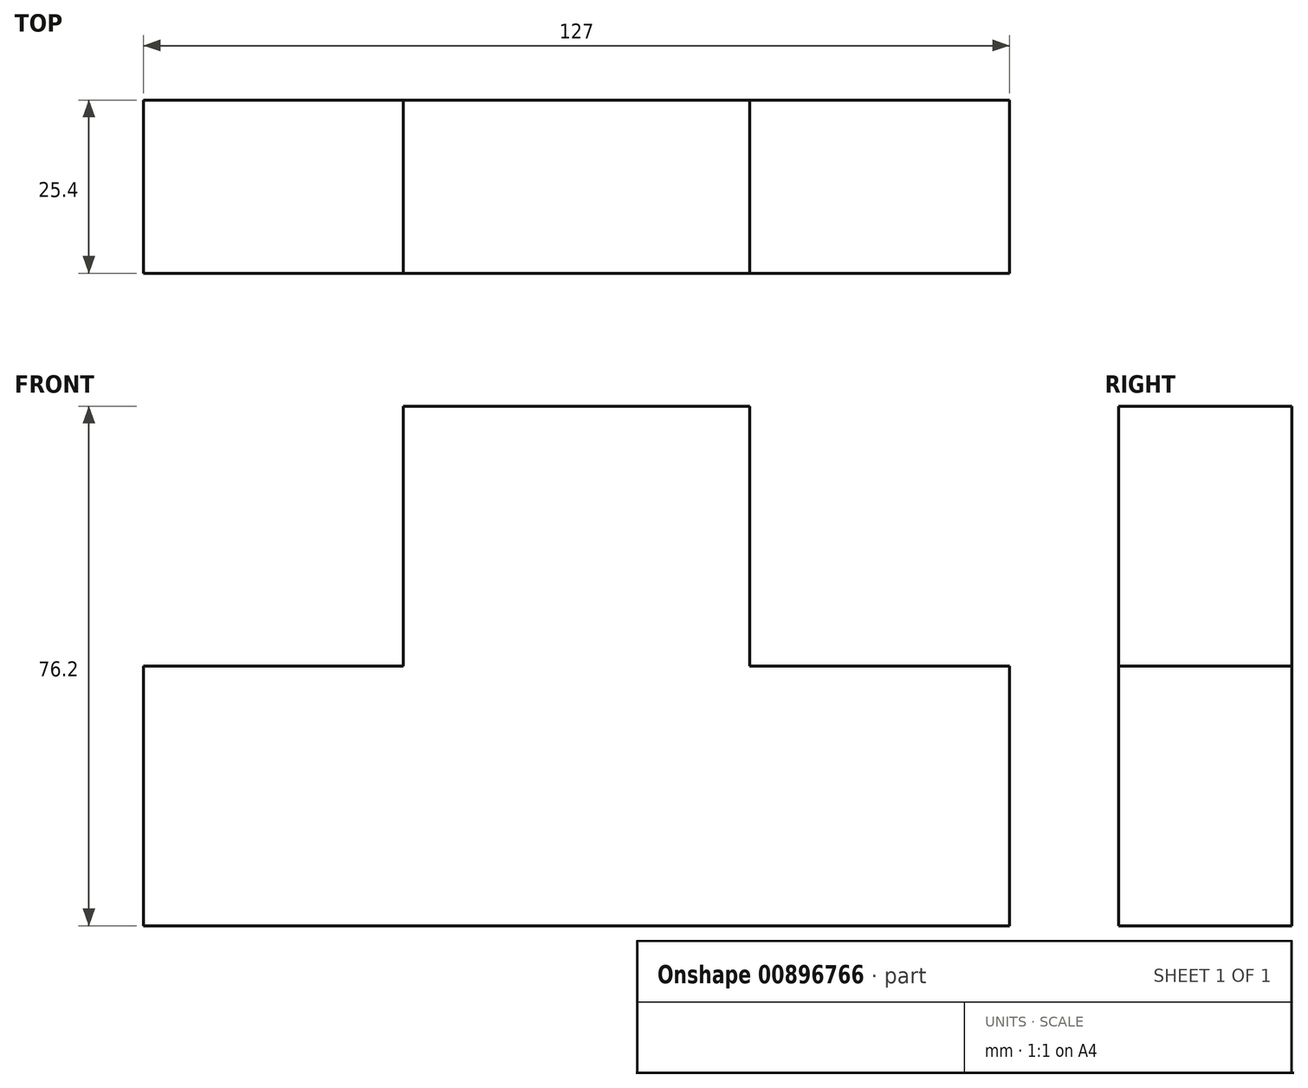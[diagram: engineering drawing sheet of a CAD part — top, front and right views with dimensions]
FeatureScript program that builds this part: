
annotation { "Feature Type Name" : "Feature", "Feature Type Description" : "" }
export const myFeature = defineFeature(function(context is Context, id is Id, definition is map)
    precondition{}
    {
        {
            var Q0;
            Q0=qCreatedBy(makeId("Front.planeOp"),FACE);
            var sketch = newSketch(context, id + "F0", { "sketchPlane" : qUnion([Q0])});
            skLineSegment(sketch, "E0.bottom", {"start": v(63.5, -19.05) * mm, "end": v(-63.5, -19.05) * mm});
            skLineSegment(sketch, "E0.top", {"start": v(63.5, 19.05) * mm, "end": v(-63.5, 19.05) * mm});
            skLineSegment(sketch, "E0.left", {"start": v(63.5, -19.05) * mm, "end": v(63.5, 19.05) * mm});
            skLineSegment(sketch, "E0.right", {"start": v(-63.5, -19.05) * mm, "end": v(-63.5, 19.05) * mm});
            skPoint(sketch, "E0.middle", {"position": v(0, 0) * mm});
            skLineSegment(sketch, "E1.bottom", {"start": v(-25.4, 57.15) * mm, "end": v(25.4, 57.15) * mm});
            skLineSegment(sketch, "E1.left", {"start": v(-25.4, 57.15) * mm, "end": v(-25.4, 19.05) * mm});
            skLineSegment(sketch, "E1.right", {"start": v(25.4, 57.15) * mm, "end": v(25.4, 19.05) * mm});
            skPoint(sketch, "E1.top.start.orphan", {"position": v(-25.4, -57.15) * mm});
            skPoint(sketch, "E2.orphan", {"position": v(25.4, -57.15) * mm});
            skSolve(sketch);
        }
        {
            var Q0;
            Q0 = qSketchRegion(id + "F0", true);
            extrude(context, id + "F1", {"entities" : qUnion([Q0]), "depth" : 25.4 * mm, "offsetDistance" : 25.4 * mm});
        }
    });
